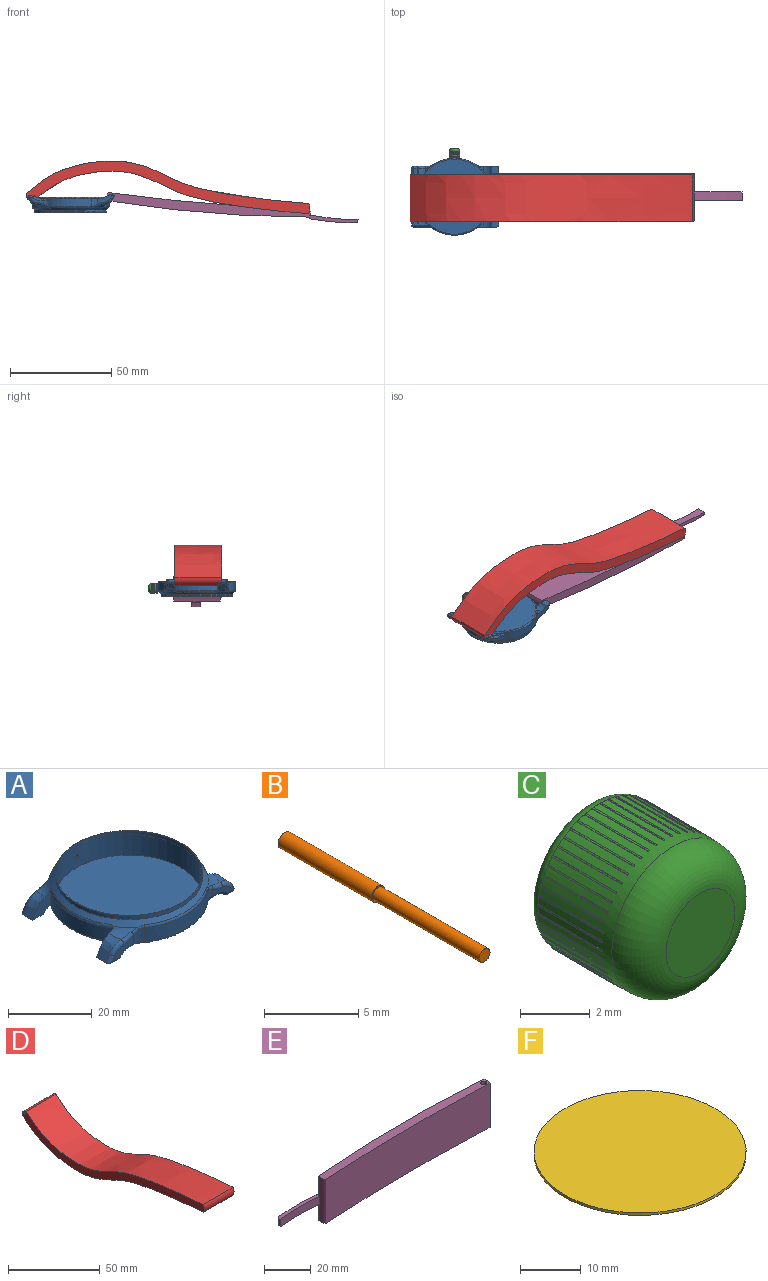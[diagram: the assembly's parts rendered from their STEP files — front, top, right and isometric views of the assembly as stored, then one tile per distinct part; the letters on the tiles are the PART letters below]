
ASSEMBLY  parts=6 mates=5
PART A: 97 faces, bbox 43.8x41.4x10.1 mm
  f0: cylinder r=19mm len=38mm, axis (0,0,-1), area 371.6mm2, adj f1,f3,f13,f14,f20,f21,f25,f27
  f1: plane 3.98x3.54mm, normal (0,0,-1), area 3.8mm2, adj f0,f2,f36,f58
  f2: plane 7.33x4.35mm, normal (0,-1,0), area 16mm2, adj f1,f4,f5,f36,f58,f88,f89,f90
  f3: plane 4.93x1.05mm, normal (-1,0,0), area 1.4mm2, adj f0,f7,f30,f32,f50,f58
  f4: plane 4.45x3.84mm, normal (0,0,-1), area 14.8mm2, adj f2,f5,f6,f7,f90
  f5: plane 4.2x0.04mm, normal (0.73,0,-0.68), area 0.2mm2, adj f2,f4,f7,f58
  f6: plane 3.21x2.46mm, normal (-0.86,0,0.51), area 8.1mm2, adj f4,f7,f54,f90
  f7: plane 6.09x5.88mm, normal (0,1,0), area 18.8mm2, adj f3,f4,f5,f6,f32,f54,f58,f95
  f8: plane 37x37mm, normal (0,0,-1), area 1075.2mm2, adj f94
  f9: plane 3.21x1.26mm, normal (0.86,0,0.51), area 3.6mm2, adj f11,f53,f69,f72
  f10: plane 3.2x1.85mm, normal (0,0,-1), area 5.9mm2, adj f11,f68,f69,f74
  f11: plane 5.88x5.49mm, normal (0,1,0), area 18.2mm2, adj f9,f10,f13,f33,f53,f56,f64,f68
  f12: plane 6.74x3.35mm, normal (0,-1,0), area 8.5mm2, adj f37,f70,f71,f72,f74,f76,f77
  f13: plane 4.93x1.05mm, normal (1,0,0), area 1.4mm2, adj f0,f11,f30,f33,f49,f56
  f14: plane 1.72x1.66mm, normal (0,0,-1), area 1.3mm2, adj f0,f56,f77,f78
  f15: plane 3.21x2.46mm, normal (-0.86,0,0.51), area 8.1mm2, adj f16,f18,f52,f93
  f16: plane 4.45x3.84mm, normal (0,0,-1), area 14.8mm2, adj f15,f17,f18,f19,f93
  f17: plane 4.2x0.04mm, normal (0.73,0,-0.68), area 0.2mm2, adj f16,f18,f19,f57
  f18: plane 6.09x5.88mm, normal (0,-1,0), area 19.3mm2, adj f15,f16,f17,f20,f31,f52,f57
  f19: plane 7.33x4.35mm, normal (0,1,0), area 16mm2, adj f16,f17,f21,f35,f57,f91,f92,f93
  f20: plane 4.93x1.05mm, normal (-1,0,0), area 1.4mm2, adj f0,f18,f30,f31,f50,f57
  f21: plane 3.98x3.54mm, normal (0,0,-1), area 3.8mm2, adj f0,f19,f35,f57
  f22: plane 3.2x1.85mm, normal (0,0,-1), area 5.9mm2, adj f24,f66,f67,f83
  f23: plane 3.21x1.26mm, normal (0.86,0,0.51), area 3.6mm2, adj f24,f51,f66,f81
  f24: plane 5.88x5.49mm, normal (0,-1,0), area 18.2mm2, adj f22,f23,f25,f34,f51,f55,f63,f66
  f25: plane 4.93x1.05mm, normal (1,0,0), area 1.4mm2, adj f0,f24,f30,f34,f49,f55
  f26: plane 6.74x3.35mm, normal (0,1,0), area 8.5mm2, adj f38,f79,f80,f81,f83,f85,f86
  f27: plane 1.72x1.66mm, normal (0,0,-1), area 1.3mm2, adj f0,f55,f86,f87
  f28: cylinder r=17.63mm len=35.27mm, axis (0,0,1), area 125.5mm2, adj f29,f30
  f29: plane 35.27x35.27mm, normal (0,0,1), area 11.5mm2, adj f28,f59
  f30: cone r=17.5mm half-angle=45deg, axis (0,0,-1), area 185mm2, adj f3,f13,f20,f25,f28,f31,f32,f33
  f31: torus R=22.57mm, axis (0,0,1), area 12.7mm2, adj f18,f20,f30,f48,f52,f91
  f32: torus R=22.57mm, axis (0,0,1), area 12.6mm2, adj f3,f7,f30,f39,f54,f88
  f33: torus R=22.57mm, axis (0,0,1), area 12.7mm2, adj f11,f13,f30,f43,f53,f70
  f34: torus R=22.57mm, axis (0,0,1), area 12.6mm2, adj f24,f25,f30,f44,f51,f79
  f35: cylinder r=5mm len=3.84mm, axis (0,0,-1), area 9.9mm2, adj f0,f19,f21,f47,f48
  f36: cylinder r=5mm len=3.84mm, axis (0,0,-1), area 9.9mm2, adj f0,f1,f2,f39,f40
  f37: cylinder r=5mm len=2.84mm, axis (0,0,-1), area 7mm2, adj f0,f12,f42,f43,f78
  f38: cylinder r=5mm len=2.84mm, axis (0,0,-1), area 7mm2, adj f0,f26,f44,f45,f87
  f39: bspline ~2.57x1.81mm, area 1.8mm2, adj f32,f36,f40,f88
  f40: bspline ~3.08x1.77mm, area 1.3mm2, adj f30,f36,f39,f41
  f41: torus R=18mm, axis (0,0,1), area 17.4mm2, adj f0,f30,f40,f42
  f42: bspline ~3.08x1.77mm, area 1.2mm2, adj f30,f37,f41,f43
  f43: bspline ~2.57x1.81mm, area 1.8mm2, adj f33,f37,f42,f70
  f44: bspline ~2.57x1.81mm, area 1.8mm2, adj f34,f38,f45,f79
  f45: bspline ~3.08x1.77mm, area 1.3mm2, adj f30,f38,f44,f46
  f46: torus R=18mm, axis (0,0,1), area 17.4mm2, adj f0,f30,f45,f47
  f47: bspline ~3.08x1.77mm, area 1.2mm2, adj f30,f35,f46,f48
  f48: bspline ~2.57x1.81mm, area 1.8mm2, adj f31,f35,f47,f91
  f49: torus R=18mm, axis (0,0,1), area 17mm2, adj f0,f13,f25,f30
  f50: torus R=18mm, axis (0,0,1), area 17mm2, adj f0,f3,f20,f30
  f51: bspline ~7.25x4.32mm, area 13.7mm2, adj f23,f24,f34,f80
  f52: bspline ~7.25x4.32mm, area 13.7mm2, adj f15,f18,f31,f92
  f53: bspline ~7.25x4.32mm, area 13.7mm2, adj f9,f11,f33,f71
  f54: bspline ~7.25x4.32mm, area 13.7mm2, adj f6,f7,f32,f89
  f55: cylinder r=5mm len=3.52mm, axis (0,-1,0), area 11.5mm2, adj f0,f24,f25,f27,f67,f85
  f56: cylinder r=5mm len=3.52mm, axis (0,-1,0), area 11.5mm2, adj f0,f11,f13,f14,f68,f76
  f57: cylinder r=5mm len=4.52mm, axis (0,-1,0), area 16.4mm2, adj f0,f17,f18,f19,f20,f21
  f58: cylinder r=5mm len=4.52mm, axis (0,-1,0), area 16.4mm2, adj f0,f1,f2,f3,f5,f7
  f59: cylinder r=17.53mm len=35.06mm, axis (0,0,1), area 781.1mm2, adj f29,f60,f61
  f60: plane 35.06x35.06mm, normal (0,0,1), area 965.3mm2, adj f59
  f61: cylinder r=0.53mm len=1.47mm, axis (0,-1,0), area 4.9mm2, adj f0,f59
  f62: plane 0.95x0.95mm, normal (0,-1,0), area 0.7mm2, adj f63
  f63: cylinder r=0.48mm len=3.11mm, axis (0,-1,0), area 9.3mm2, adj f24,f62
  f64: cylinder r=0.48mm len=2.9mm, axis (0,-1,0), area 8.7mm2, adj f11,f65
  f65: plane 0.95x0.95mm, normal (0,1,0), area 0.7mm2, adj f64
  f66: cylinder r=0.8mm len=3.2mm, axis (0,1,0), area 5.4mm2, adj f22,f23,f24,f82
  f67: cylinder r=0.8mm len=3.2mm, axis (0,-1,0), area 2mm2, adj f22,f24,f55,f84
  f68: cylinder r=0.8mm len=3.2mm, axis (0,-1,0), area 2mm2, adj f10,f11,f56,f75
  f69: cylinder r=0.8mm len=3.2mm, axis (0,1,0), area 5.4mm2, adj f9,f10,f11,f73
  f70: bspline ~4.82x1.97mm, area 4.5mm2, adj f12,f33,f43,f71
  f71: bspline ~4.93x3.72mm, area 6.7mm2, adj f12,f53,f70,f72
  f72: cylinder r=1mm len=1.31mm, axis (-0.51,0,0.86), area 1.1mm2, adj f9,f12,f71,f73
  f73: bspline ~1.75x1.21mm, area 1.3mm2, adj f69,f72,f74
  f74: cylinder r=1mm len=1.85mm, axis (1,0,0), area 2.6mm2, adj f10,f12,f73,f75
  f75: bspline ~1.24x1mm, area 0.4mm2, adj f68,f74,f76
  f76: torus R=6mm, axis (0,-1,0), area 6.4mm2, adj f12,f56,f75,f77
  f77: cylinder r=1mm len=1.22mm, axis (-1,0,0), area 1.9mm2, adj f12,f14,f76,f78
  f78: torus R=6mm, axis (0,0,-1), area 2.7mm2, adj f0,f14,f37,f77
  f79: bspline ~4.82x1.97mm, area 4.5mm2, adj f26,f34,f44,f80
  f80: bspline ~4.93x3.72mm, area 6.7mm2, adj f26,f51,f79,f81
  f81: cylinder r=1mm len=1.31mm, axis (0.51,0,-0.86), area 1.1mm2, adj f23,f26,f80,f82
  f82: bspline ~1.75x1.21mm, area 1.3mm2, adj f66,f81,f83
  f83: cylinder r=1mm len=1.85mm, axis (-1,0,0), area 2.6mm2, adj f22,f26,f82,f84
  f84: bspline ~1.24x1mm, area 0.4mm2, adj f67,f83,f85
  f85: torus R=6mm, axis (0,-1,0), area 6.4mm2, adj f26,f55,f84,f86
  f86: cylinder r=1mm len=1.22mm, axis (1,0,0), area 1.9mm2, adj f26,f27,f85,f87
  f87: torus R=6mm, axis (0,0,-1), area 2.7mm2, adj f0,f27,f38,f86
  f88: bspline ~4.82x1.97mm, area 4.5mm2, adj f2,f32,f39,f89
  f89: bspline ~4.97x3.81mm, area 6.7mm2, adj f2,f54,f88,f90
  f90: cylinder r=1mm len=2.48mm, axis (0.51,0,0.86), area 3.1mm2, adj f2,f4,f6,f89
  f91: bspline ~4.82x1.97mm, area 4.5mm2, adj f19,f31,f48,f92
  f92: bspline ~4.97x3.81mm, area 6.7mm2, adj f19,f52,f91,f93
  f93: cylinder r=1mm len=2.48mm, axis (-0.51,0,-0.86), area 3.1mm2, adj f15,f16,f19,f92
  f94: torus R=18.5mm, axis (0,0,1), area 92.9mm2, adj f0,f8
  f95: cylinder r=0.41mm len=3mm, axis (0,1,0), area 7.6mm2, adj f7,f96
  f96: plane 0.81x0.81mm, normal (0,1,0), area 0.5mm2, adj f95
PART B: 5 faces, bbox 1x15x1 mm
  f0: cylinder r=0.5mm len=7mm, axis (0,1,0), area 21.9mm2, adj f1,f3
  f1: plane 1x1mm, normal (0,1,0), area 0.8mm2, adj f0
  f2: cylinder r=0.42mm len=8mm, axis (0,-1,0), area 20.9mm2, adj f3,f4
  f3: plane 1x1mm, normal (0,-1,0), area 0.2mm2, adj f0,f2
  f4: plane 0.83x0.83mm, normal (0,-1,0), area 0.5mm2, adj f2
PART C: 257 faces, bbox 5.4x4.5x5.4 mm
  f0: cylinder r=2.5mm len=5mm, axis (0,1,0), area 40.6mm2, adj f3,f4,f7,f8,f9,f11,f12,f13
  f1: plane 2.8x2.8mm, normal (0,-1,0), area 6.2mm2, adj f3
  f2: plane 4.2x4.2mm, normal (0,1,0), area 13.1mm2, adj f4,f5
  f3: torus R=1.4mm, axis (0,-1,0), area 22.8mm2, adj f0,f1
  f4: torus R=2.1mm, axis (0,-1,0), area 9.3mm2, adj f0,f2
  f5: cylinder r=0.5mm len=3mm, axis (0,1,0), area 9.4mm2, adj f2,f6
  f6: plane 1x1mm, normal (0,1,0), area 0.8mm2, adj f5
  f7: plane 2.6x0.02mm, normal (1,0,0), area 0.1mm2, adj f0,f9,f10,f11
  f8: plane 2.6x0.02mm, normal (-1,0,0), area 0mm2, adj f0,f9,f10,f11
  f9: plane 0.05x0.02mm, normal (0,1,0), area 0mm2, adj f0,f7,f8,f10
  f10: plane 2.6x0.05mm, normal (0,0,1), area 0.1mm2, adj f7,f8,f9,f11
  f11: plane 0.05x0.02mm, normal (0,-1,0), area 0mm2, adj f0,f7,f8,f10
  f12: plane 2.6x0.02mm, normal (0.99,0,0.13), area 0.1mm2, adj f0,f14,f15,f16
  f13: plane 2.6x0.02mm, normal (-0.99,0,-0.13), area 0mm2, adj f0,f14,f15,f16
  f14: plane 0.05x0.03mm, normal (0,1,0), area 0mm2, adj f0,f12,f13,f15
  f15: plane 2.6x0.05mm, normal (-0.13,0,0.99), area 0.1mm2, adj f12,f13,f14,f16
  f16: plane 0.05x0.03mm, normal (0,-1,0), area 0mm2, adj f0,f12,f13,f15
  f17: plane 2.6x0.02mm, normal (0.97,0,0.25), area 0.1mm2, adj f0,f19,f20,f21
  f18: plane 2.6x0.02mm, normal (-0.97,0,-0.25), area 0mm2, adj f0,f19,f20,f21
  f19: plane 0.05x0.03mm, normal (0,1,0), area 0mm2, adj f0,f17,f18,f20
  f20: plane 2.6x0.05mm, normal (-0.25,0,0.97), area 0.1mm2, adj f17,f18,f19,f21
  f21: plane 0.05x0.03mm, normal (0,-1,0), area 0mm2, adj f0,f17,f18,f20
  f22: plane 2.6x0.02mm, normal (0.93,0,0.37), area 0.1mm2, adj f0,f24,f25,f26
  f23: plane 2.6x0.02mm, normal (-0.93,0,-0.37), area 0mm2, adj f0,f24,f25,f26
  f24: plane 0.05x0.04mm, normal (0,1,0), area 0mm2, adj f0,f22,f23,f25
  f25: plane 2.6x0.05mm, normal (-0.37,0,0.93), area 0.1mm2, adj f22,f23,f24,f26
  f26: plane 0.05x0.04mm, normal (0,-1,0), area 0mm2, adj f0,f22,f23,f25
  f27: plane 2.6x0.02mm, normal (0.88,0,0.48), area 0.1mm2, adj f0,f29,f30,f31
  f28: plane 2.6x0.02mm, normal (-0.88,0,-0.48), area 0mm2, adj f0,f29,f30,f31
  f29: plane 0.05x0.04mm, normal (0,1,0), area 0mm2, adj f0,f27,f28,f30
  f30: plane 2.6x0.04mm, normal (-0.48,0,0.88), area 0.1mm2, adj f27,f28,f29,f31
  f31: plane 0.05x0.04mm, normal (0,-1,0), area 0mm2, adj f0,f27,f28,f30
  f32: plane 2.6x0.02mm, normal (0.81,0,0.59), area 0.1mm2, adj f0,f34,f35,f36
  f33: plane 2.6x0.02mm, normal (-0.81,0,-0.59), area 0mm2, adj f0,f34,f35,f36
  f34: plane 0.05x0.04mm, normal (0,1,0), area 0mm2, adj f0,f32,f33,f35
  f35: plane 2.6x0.04mm, normal (-0.59,0,0.81), area 0.1mm2, adj f32,f33,f34,f36
  f36: plane 0.05x0.04mm, normal (0,-1,0), area 0mm2, adj f0,f32,f33,f35
  f37: plane 2.6x0.01mm, normal (0.73,0,0.68), area 0.1mm2, adj f0,f39,f40,f41
  f38: plane 2.6x0.01mm, normal (-0.73,0,-0.68), area 0mm2, adj f0,f39,f40,f41
  f39: plane 0.05x0.05mm, normal (0,1,0), area 0mm2, adj f0,f37,f38,f40
  f40: plane 2.6x0.04mm, normal (-0.68,0,0.73), area 0.1mm2, adj f37,f38,f39,f41
  f41: plane 0.05x0.05mm, normal (0,-1,0), area 0mm2, adj f0,f37,f38,f40
  f42: plane 2.6x0.02mm, normal (0.64,0,0.77), area 0.1mm2, adj f0,f44,f45,f46
  f43: plane 2.6x0.01mm, normal (-0.64,0,-0.77), area 0mm2, adj f0,f44,f45,f46
  f44: plane 0.05x0.05mm, normal (0,1,0), area 0mm2, adj f0,f42,f43,f45
  f45: plane 2.6x0.04mm, normal (-0.77,0,0.64), area 0.1mm2, adj f42,f43,f44,f46
  f46: plane 0.05x0.05mm, normal (0,-1,0), area 0mm2, adj f0,f42,f43,f45
  f47: plane 2.6x0.02mm, normal (0.54,0,0.84), area 0.1mm2, adj f0,f49,f50,f51
  f48: plane 2.6x0.02mm, normal (-0.54,0,-0.84), area 0mm2, adj f0,f49,f50,f51
  f49: plane 0.05x0.04mm, normal (0,1,0), area 0mm2, adj f0,f47,f48,f50
  f50: plane 2.6x0.04mm, normal (-0.84,0,0.54), area 0.1mm2, adj f47,f48,f49,f51
  f51: plane 0.05x0.04mm, normal (0,-1,0), area 0mm2, adj f0,f47,f48,f50
  f52: plane 2.6x0.02mm, normal (0.43,0,0.9), area 0.1mm2, adj f0,f54,f55,f56
  f53: plane 2.6x0.02mm, normal (-0.43,0,-0.9), area 0mm2, adj f0,f54,f55,f56
  f54: plane 0.05x0.04mm, normal (0,1,0), area 0mm2, adj f0,f52,f53,f55
  f55: plane 2.6x0.05mm, normal (-0.9,0,0.43), area 0.1mm2, adj f52,f53,f54,f56
  f56: plane 0.05x0.04mm, normal (0,-1,0), area 0mm2, adj f0,f52,f53,f55
  f57: plane 2.6x0.02mm, normal (0.31,0,0.95), area 0.1mm2, adj f0,f59,f60,f61
  f58: plane 2.6x0.02mm, normal (-0.31,0,-0.95), area 0mm2, adj f0,f59,f60,f61
  f59: plane 0.05x0.03mm, normal (0,1,0), area 0mm2, adj f0,f57,f58,f60
  f60: plane 2.6x0.05mm, normal (-0.95,0,0.31), area 0.1mm2, adj f57,f58,f59,f61
  f61: plane 0.05x0.03mm, normal (0,-1,0), area 0mm2, adj f0,f57,f58,f60
  f62: plane 2.6x0.02mm, normal (0.19,0,0.98), area 0.1mm2, adj f0,f64,f65,f66
  f63: plane 2.6x0.02mm, normal (-0.19,0,-0.98), area 0mm2, adj f0,f64,f65,f66
  f64: plane 0.05x0.03mm, normal (0,1,0), area 0mm2, adj f0,f62,f63,f65
  f65: plane 2.6x0.05mm, normal (-0.98,0,0.19), area 0.1mm2, adj f62,f63,f64,f66
  f66: plane 0.05x0.03mm, normal (0,-1,0), area 0mm2, adj f0,f62,f63,f65
  f67: plane 2.6x0.02mm, normal (0.06,0,1), area 0.1mm2, adj f0,f69,f70,f71
  f68: plane 2.6x0.02mm, normal (-0.06,0,-1), area 0mm2, adj f0,f69,f70,f71
  f69: plane 0.05x0.02mm, normal (0,1,0), area 0mm2, adj f0,f67,f68,f70
  f70: plane 2.6x0.05mm, normal (-1,0,0.06), area 0.1mm2, adj f67,f68,f69,f71
  f71: plane 0.05x0.02mm, normal (0,-1,0), area 0mm2, adj f0,f67,f68,f70
  f72: plane 2.6x0.02mm, normal (-0.06,0,1), area 0.1mm2, adj f0,f74,f75,f76
  f73: plane 2.6x0.02mm, normal (0.06,0,-1), area 0mm2, adj f0,f74,f75,f76
  f74: plane 0.05x0.02mm, normal (0,1,0), area 0mm2, adj f0,f72,f73,f75
  f75: plane 2.6x0.05mm, normal (-1,0,-0.06), area 0.1mm2, adj f72,f73,f74,f76
  f76: plane 0.05x0.02mm, normal (0,-1,0), area 0mm2, adj f0,f72,f73,f75
  f77: plane 2.6x0.02mm, normal (-0.19,0,0.98), area 0.1mm2, adj f0,f79,f80,f81
  f78: plane 2.6x0.02mm, normal (0.19,0,-0.98), area 0mm2, adj f0,f79,f80,f81
  f79: plane 0.05x0.03mm, normal (0,1,0), area 0mm2, adj f0,f77,f78,f80
  f80: plane 2.6x0.05mm, normal (-0.98,0,-0.19), area 0.1mm2, adj f77,f78,f79,f81
  f81: plane 0.05x0.03mm, normal (0,-1,0), area 0mm2, adj f0,f77,f78,f80
  f82: plane 2.6x0.02mm, normal (-0.31,0,0.95), area 0.1mm2, adj f0,f84,f85,f86
  f83: plane 2.6x0.02mm, normal (0.31,0,-0.95), area 0mm2, adj f0,f84,f85,f86
  f84: plane 0.05x0.03mm, normal (0,1,0), area 0mm2, adj f0,f82,f83,f85
  f85: plane 2.6x0.05mm, normal (-0.95,0,-0.31), area 0.1mm2, adj f82,f83,f84,f86
  f86: plane 0.05x0.03mm, normal (0,-1,0), area 0mm2, adj f0,f82,f83,f85
  f87: plane 2.6x0.02mm, normal (-0.43,0,0.9), area 0.1mm2, adj f0,f89,f90,f91
  f88: plane 2.6x0.02mm, normal (0.43,0,-0.9), area 0mm2, adj f0,f89,f90,f91
  f89: plane 0.05x0.04mm, normal (0,1,0), area 0mm2, adj f0,f87,f88,f90
  f90: plane 2.6x0.05mm, normal (-0.9,0,-0.43), area 0.1mm2, adj f87,f88,f89,f91
  f91: plane 0.05x0.04mm, normal (0,-1,0), area 0mm2, adj f0,f87,f88,f90
  f92: plane 2.6x0.02mm, normal (-0.54,0,0.84), area 0.1mm2, adj f0,f94,f95,f96
  f93: plane 2.6x0.02mm, normal (0.54,0,-0.84), area 0mm2, adj f0,f94,f95,f96
  f94: plane 0.05x0.04mm, normal (0,1,0), area 0mm2, adj f0,f92,f93,f95
  f95: plane 2.6x0.04mm, normal (-0.84,0,-0.54), area 0.1mm2, adj f92,f93,f94,f96
  f96: plane 0.05x0.04mm, normal (0,-1,0), area 0mm2, adj f0,f92,f93,f95
  f97: plane 2.6x0.02mm, normal (-0.64,0,0.77), area 0.1mm2, adj f0,f99,f100,f101
  f98: plane 2.6x0.01mm, normal (0.64,0,-0.77), area 0mm2, adj f0,f99,f100,f101
  f99: plane 0.05x0.05mm, normal (0,1,0), area 0mm2, adj f0,f97,f98,f100
  f100: plane 2.6x0.04mm, normal (-0.77,0,-0.64), area 0.1mm2, adj f97,f98,f99,f101
  f101: plane 0.05x0.05mm, normal (0,-1,0), area 0mm2, adj f0,f97,f98,f100
  f102: plane 2.6x0.01mm, normal (-0.73,0,0.68), area 0.1mm2, adj f0,f104,f105,f106
  f103: plane 2.6x0.01mm, normal (0.73,0,-0.68), area 0mm2, adj f0,f104,f105,f106
  f104: plane 0.05x0.05mm, normal (0,1,0), area 0mm2, adj f0,f102,f103,f105
  f105: plane 2.6x0.04mm, normal (-0.68,0,-0.73), area 0.1mm2, adj f102,f103,f104,f106
  f106: plane 0.05x0.05mm, normal (0,-1,0), area 0mm2, adj f0,f102,f103,f105
  f107: plane 2.6x0.02mm, normal (-0.81,0,0.59), area 0.1mm2, adj f0,f109,f110,f111
  f108: plane 2.6x0.02mm, normal (0.81,0,-0.59), area 0mm2, adj f0,f109,f110,f111
  f109: plane 0.05x0.05mm, normal (0,1,0), area 0mm2, adj f0,f107,f108,f110
  f110: plane 2.6x0.04mm, normal (-0.59,0,-0.81), area 0.1mm2, adj f107,f108,f109,f111
  f111: plane 0.05x0.05mm, normal (0,-1,0), area 0mm2, adj f0,f107,f108,f110
  f112: plane 2.6x0.02mm, normal (-0.88,0,0.48), area 0.1mm2, adj f0,f114,f115,f116
  f113: plane 2.6x0.02mm, normal (0.88,0,-0.48), area 0mm2, adj f0,f114,f115,f116
  f114: plane 0.05x0.04mm, normal (0,1,0), area 0mm2, adj f0,f112,f113,f115
  f115: plane 2.6x0.04mm, normal (-0.48,0,-0.88), area 0.1mm2, adj f112,f113,f114,f116
  f116: plane 0.05x0.04mm, normal (0,-1,0), area 0mm2, adj f0,f112,f113,f115
  f117: plane 2.6x0.02mm, normal (-0.93,0,0.37), area 0.1mm2, adj f0,f119,f120,f121
  f118: plane 2.6x0.02mm, normal (0.93,0,-0.37), area 0mm2, adj f0,f119,f120,f121
  f119: plane 0.05x0.04mm, normal (0,1,0), area 0mm2, adj f0,f117,f118,f120
  f120: plane 2.6x0.05mm, normal (-0.37,0,-0.93), area 0.1mm2, adj f117,f118,f119,f121
  f121: plane 0.05x0.04mm, normal (0,-1,0), area 0mm2, adj f0,f117,f118,f120
  f122: plane 2.6x0.02mm, normal (-0.97,0,0.25), area 0.1mm2, adj f0,f124,f125,f126
  f123: plane 2.6x0.02mm, normal (0.97,0,-0.25), area 0mm2, adj f0,f124,f125,f126
  f124: plane 0.05x0.03mm, normal (0,1,0), area 0mm2, adj f0,f122,f123,f125
  f125: plane 2.6x0.05mm, normal (-0.25,0,-0.97), area 0.1mm2, adj f122,f123,f124,f126
  f126: plane 0.05x0.03mm, normal (0,-1,0), area 0mm2, adj f0,f122,f123,f125
  f127: plane 2.6x0.02mm, normal (-0.99,0,0.13), area 0.1mm2, adj f0,f129,f130,f131
  f128: plane 2.6x0.02mm, normal (0.99,0,-0.13), area 0mm2, adj f0,f129,f130,f131
  f129: plane 0.05x0.03mm, normal (0,1,0), area 0mm2, adj f0,f127,f128,f130
  f130: plane 2.6x0.05mm, normal (-0.13,0,-0.99), area 0.1mm2, adj f127,f128,f129,f131
  f131: plane 0.05x0.03mm, normal (0,-1,0), area 0mm2, adj f0,f127,f128,f130
  f132: plane 2.6x0.02mm, normal (-1,0,0), area 0.1mm2, adj f0,f134,f135,f136
  f133: plane 2.6x0.02mm, normal (1,0,0), area 0mm2, adj f0,f134,f135,f136
  f134: plane 0.05x0.02mm, normal (0,1,0), area 0mm2, adj f0,f132,f133,f135
  f135: plane 2.6x0.05mm, normal (0,0,-1), area 0.1mm2, adj f132,f133,f134,f136
  f136: plane 0.05x0.02mm, normal (0,-1,0), area 0mm2, adj f0,f132,f133,f135
  f137: plane 2.6x0.02mm, normal (-0.99,0,-0.13), area 0.1mm2, adj f0,f139,f140,f141
  f138: plane 2.6x0.02mm, normal (0.99,0,0.13), area 0mm2, adj f0,f139,f140,f141
  f139: plane 0.05x0.03mm, normal (0,1,0), area 0mm2, adj f0,f137,f138,f140
  f140: plane 2.6x0.05mm, normal (0.13,0,-0.99), area 0.1mm2, adj f137,f138,f139,f141
  f141: plane 0.05x0.03mm, normal (0,-1,0), area 0mm2, adj f0,f137,f138,f140
  f142: plane 2.6x0.02mm, normal (-0.97,0,-0.25), area 0.1mm2, adj f0,f144,f145,f146
  f143: plane 2.6x0.02mm, normal (0.97,0,0.25), area 0mm2, adj f0,f144,f145,f146
  f144: plane 0.05x0.03mm, normal (0,1,0), area 0mm2, adj f0,f142,f143,f145
  f145: plane 2.6x0.05mm, normal (0.25,0,-0.97), area 0.1mm2, adj f142,f143,f144,f146
  f146: plane 0.05x0.03mm, normal (0,-1,0), area 0mm2, adj f0,f142,f143,f145
  f147: plane 2.6x0.02mm, normal (-0.93,0,-0.37), area 0.1mm2, adj f0,f149,f150,f151
  f148: plane 2.6x0.02mm, normal (0.93,0,0.37), area 0mm2, adj f0,f149,f150,f151
  f149: plane 0.05x0.04mm, normal (0,1,0), area 0mm2, adj f0,f147,f148,f150
  f150: plane 2.6x0.05mm, normal (0.37,0,-0.93), area 0.1mm2, adj f147,f148,f149,f151
  f151: plane 0.05x0.04mm, normal (0,-1,0), area 0mm2, adj f0,f147,f148,f150
  f152: plane 2.6x0.02mm, normal (-0.88,0,-0.48), area 0.1mm2, adj f0,f154,f155,f156
  f153: plane 2.6x0.02mm, normal (0.88,0,0.48), area 0mm2, adj f0,f154,f155,f156
  f154: plane 0.05x0.04mm, normal (0,1,0), area 0mm2, adj f0,f152,f153,f155
  f155: plane 2.6x0.04mm, normal (0.48,0,-0.88), area 0.1mm2, adj f152,f153,f154,f156
  f156: plane 0.05x0.04mm, normal (0,-1,0), area 0mm2, adj f0,f152,f153,f155
  f157: plane 2.6x0.02mm, normal (-0.81,0,-0.59), area 0.1mm2, adj f0,f159,f160,f161
  f158: plane 2.6x0.02mm, normal (0.81,0,0.59), area 0mm2, adj f0,f159,f160,f161
  f159: plane 0.05x0.04mm, normal (0,1,0), area 0mm2, adj f0,f157,f158,f160
  f160: plane 2.6x0.04mm, normal (0.59,0,-0.81), area 0.1mm2, adj f157,f158,f159,f161
  f161: plane 0.05x0.04mm, normal (0,-1,0), area 0mm2, adj f0,f157,f158,f160
  f162: plane 2.6x0.01mm, normal (-0.73,0,-0.68), area 0.1mm2, adj f0,f164,f165,f166
  f163: plane 2.6x0.01mm, normal (0.73,0,0.68), area 0mm2, adj f0,f164,f165,f166
  f164: plane 0.05x0.05mm, normal (0,1,0), area 0mm2, adj f0,f162,f163,f165
  f165: plane 2.6x0.04mm, normal (0.68,0,-0.73), area 0.1mm2, adj f162,f163,f164,f166
  f166: plane 0.05x0.05mm, normal (0,-1,0), area 0mm2, adj f0,f162,f163,f165
  f167: plane 2.6x0.02mm, normal (-0.64,0,-0.77), area 0.1mm2, adj f0,f169,f170,f171
  f168: plane 2.6x0.01mm, normal (0.64,0,0.77), area 0mm2, adj f0,f169,f170,f171
  f169: plane 0.05x0.05mm, normal (0,1,0), area 0mm2, adj f0,f167,f168,f170
  f170: plane 2.6x0.04mm, normal (0.77,0,-0.64), area 0.1mm2, adj f167,f168,f169,f171
  f171: plane 0.05x0.05mm, normal (0,-1,0), area 0mm2, adj f0,f167,f168,f170
  f172: plane 2.6x0.02mm, normal (-0.54,0,-0.84), area 0.1mm2, adj f0,f174,f175,f176
  f173: plane 2.6x0.02mm, normal (0.54,0,0.84), area 0mm2, adj f0,f174,f175,f176
  f174: plane 0.05x0.04mm, normal (0,1,0), area 0mm2, adj f0,f172,f173,f175
  f175: plane 2.6x0.04mm, normal (0.84,0,-0.54), area 0.1mm2, adj f172,f173,f174,f176
  f176: plane 0.05x0.04mm, normal (0,-1,0), area 0mm2, adj f0,f172,f173,f175
  f177: plane 2.6x0.02mm, normal (-0.43,0,-0.9), area 0.1mm2, adj f0,f179,f180,f181
  f178: plane 2.6x0.02mm, normal (0.43,0,0.9), area 0mm2, adj f0,f179,f180,f181
  f179: plane 0.05x0.04mm, normal (0,1,0), area 0mm2, adj f0,f177,f178,f180
  f180: plane 2.6x0.05mm, normal (0.9,0,-0.43), area 0.1mm2, adj f177,f178,f179,f181
  f181: plane 0.05x0.04mm, normal (0,-1,0), area 0mm2, adj f0,f177,f178,f180
  f182: plane 2.6x0.02mm, normal (-0.31,0,-0.95), area 0.1mm2, adj f0,f184,f185,f186
  f183: plane 2.6x0.02mm, normal (0.31,0,0.95), area 0mm2, adj f0,f184,f185,f186
  f184: plane 0.05x0.03mm, normal (0,1,0), area 0mm2, adj f0,f182,f183,f185
  f185: plane 2.6x0.05mm, normal (0.95,0,-0.31), area 0.1mm2, adj f182,f183,f184,f186
  f186: plane 0.05x0.03mm, normal (0,-1,0), area 0mm2, adj f0,f182,f183,f185
  f187: plane 2.6x0.02mm, normal (-0.19,0,-0.98), area 0.1mm2, adj f0,f189,f190,f191
  f188: plane 2.6x0.02mm, normal (0.19,0,0.98), area 0mm2, adj f0,f189,f190,f191
  f189: plane 0.05x0.03mm, normal (0,1,0), area 0mm2, adj f0,f187,f188,f190
  f190: plane 2.6x0.05mm, normal (0.98,0,-0.19), area 0.1mm2, adj f187,f188,f189,f191
  f191: plane 0.05x0.03mm, normal (0,-1,0), area 0mm2, adj f0,f187,f188,f190
  f192: plane 2.6x0.02mm, normal (-0.06,0,-1), area 0.1mm2, adj f0,f194,f195,f196
  f193: plane 2.6x0.02mm, normal (0.06,0,1), area 0mm2, adj f0,f194,f195,f196
  f194: plane 0.05x0.02mm, normal (0,1,0), area 0mm2, adj f0,f192,f193,f195
  f195: plane 2.6x0.05mm, normal (1,0,-0.06), area 0.1mm2, adj f192,f193,f194,f196
  f196: plane 0.05x0.02mm, normal (0,-1,0), area 0mm2, adj f0,f192,f193,f195
  f197: plane 2.6x0.02mm, normal (0.06,0,-1), area 0.1mm2, adj f0,f199,f200,f201
  f198: plane 2.6x0.02mm, normal (-0.06,0,1), area 0mm2, adj f0,f199,f200,f201
  f199: plane 0.05x0.02mm, normal (0,1,0), area 0mm2, adj f0,f197,f198,f200
  f200: plane 2.6x0.05mm, normal (1,0,0.06), area 0.1mm2, adj f197,f198,f199,f201
  f201: plane 0.05x0.02mm, normal (0,-1,0), area 0mm2, adj f0,f197,f198,f200
  f202: plane 2.6x0.02mm, normal (0.19,0,-0.98), area 0.1mm2, adj f0,f204,f205,f206
  f203: plane 2.6x0.02mm, normal (-0.19,0,0.98), area 0mm2, adj f0,f204,f205,f206
  f204: plane 0.05x0.03mm, normal (0,1,0), area 0mm2, adj f0,f202,f203,f205
  f205: plane 2.6x0.05mm, normal (0.98,0,0.19), area 0.1mm2, adj f202,f203,f204,f206
  f206: plane 0.05x0.03mm, normal (0,-1,0), area 0mm2, adj f0,f202,f203,f205
  f207: plane 2.6x0.02mm, normal (0.31,0,-0.95), area 0.1mm2, adj f0,f209,f210,f211
  f208: plane 2.6x0.02mm, normal (-0.31,0,0.95), area 0mm2, adj f0,f209,f210,f211
  f209: plane 0.05x0.03mm, normal (0,1,0), area 0mm2, adj f0,f207,f208,f210
  f210: plane 2.6x0.05mm, normal (0.95,0,0.31), area 0.1mm2, adj f207,f208,f209,f211
  f211: plane 0.05x0.03mm, normal (0,-1,0), area 0mm2, adj f0,f207,f208,f210
  f212: plane 2.6x0.02mm, normal (0.43,0,-0.9), area 0.1mm2, adj f0,f214,f215,f216
  f213: plane 2.6x0.02mm, normal (-0.43,0,0.9), area 0mm2, adj f0,f214,f215,f216
  f214: plane 0.05x0.04mm, normal (0,1,0), area 0mm2, adj f0,f212,f213,f215
  f215: plane 2.6x0.05mm, normal (0.9,0,0.43), area 0.1mm2, adj f212,f213,f214,f216
  f216: plane 0.05x0.04mm, normal (0,-1,0), area 0mm2, adj f0,f212,f213,f215
  f217: plane 2.6x0.02mm, normal (0.54,0,-0.84), area 0.1mm2, adj f0,f219,f220,f221
  f218: plane 2.6x0.02mm, normal (-0.54,0,0.84), area 0mm2, adj f0,f219,f220,f221
  f219: plane 0.05x0.04mm, normal (0,1,0), area 0mm2, adj f0,f217,f218,f220
  f220: plane 2.6x0.04mm, normal (0.84,0,0.54), area 0.1mm2, adj f217,f218,f219,f221
  f221: plane 0.05x0.04mm, normal (0,-1,0), area 0mm2, adj f0,f217,f218,f220
  f222: plane 2.6x0.02mm, normal (0.64,0,-0.77), area 0.1mm2, adj f0,f224,f225,f226
  f223: plane 2.6x0.01mm, normal (-0.64,0,0.77), area 0mm2, adj f0,f224,f225,f226
  f224: plane 0.05x0.05mm, normal (0,1,0), area 0mm2, adj f0,f222,f223,f225
  f225: plane 2.6x0.04mm, normal (0.77,0,0.64), area 0.1mm2, adj f222,f223,f224,f226
  f226: plane 0.05x0.05mm, normal (0,-1,0), area 0mm2, adj f0,f222,f223,f225
  f227: plane 2.6x0.01mm, normal (0.73,0,-0.68), area 0.1mm2, adj f0,f229,f230,f231
  f228: plane 2.6x0.01mm, normal (-0.73,0,0.68), area 0mm2, adj f0,f229,f230,f231
  f229: plane 0.05x0.05mm, normal (0,1,0), area 0mm2, adj f0,f227,f228,f230
  f230: plane 2.6x0.04mm, normal (0.68,0,0.73), area 0.1mm2, adj f227,f228,f229,f231
  f231: plane 0.05x0.05mm, normal (0,-1,0), area 0mm2, adj f0,f227,f228,f230
  f232: plane 2.6x0.02mm, normal (0.81,0,-0.59), area 0.1mm2, adj f0,f234,f235,f236
  f233: plane 2.6x0.02mm, normal (-0.81,0,0.59), area 0mm2, adj f0,f234,f235,f236
  f234: plane 0.05x0.05mm, normal (0,1,0), area 0mm2, adj f0,f232,f233,f235
  f235: plane 2.6x0.04mm, normal (0.59,0,0.81), area 0.1mm2, adj f232,f233,f234,f236
  f236: plane 0.05x0.05mm, normal (0,-1,0), area 0mm2, adj f0,f232,f233,f235
  f237: plane 2.6x0.02mm, normal (0.88,0,-0.48), area 0.1mm2, adj f0,f239,f240,f241
  f238: plane 2.6x0.02mm, normal (-0.88,0,0.48), area 0mm2, adj f0,f239,f240,f241
  f239: plane 0.05x0.04mm, normal (0,1,0), area 0mm2, adj f0,f237,f238,f240
  f240: plane 2.6x0.04mm, normal (0.48,0,0.88), area 0.1mm2, adj f237,f238,f239,f241
  f241: plane 0.05x0.04mm, normal (0,-1,0), area 0mm2, adj f0,f237,f238,f240
  f242: plane 2.6x0.02mm, normal (0.93,0,-0.37), area 0.1mm2, adj f0,f244,f245,f246
  f243: plane 2.6x0.02mm, normal (-0.93,0,0.37), area 0mm2, adj f0,f244,f245,f246
  f244: plane 0.05x0.04mm, normal (0,1,0), area 0mm2, adj f0,f242,f243,f245
  f245: plane 2.6x0.05mm, normal (0.37,0,0.93), area 0.1mm2, adj f242,f243,f244,f246
  f246: plane 0.05x0.04mm, normal (0,-1,0), area 0mm2, adj f0,f242,f243,f245
  f247: plane 2.6x0.02mm, normal (0.97,0,-0.25), area 0.1mm2, adj f0,f249,f250,f251
  f248: plane 2.6x0.02mm, normal (-0.97,0,0.25), area 0mm2, adj f0,f249,f250,f251
  f249: plane 0.05x0.03mm, normal (0,1,0), area 0mm2, adj f0,f247,f248,f250
  f250: plane 2.6x0.05mm, normal (0.25,0,0.97), area 0.1mm2, adj f247,f248,f249,f251
  f251: plane 0.05x0.03mm, normal (0,-1,0), area 0mm2, adj f0,f247,f248,f250
  f252: plane 2.6x0.02mm, normal (0.99,0,-0.13), area 0.1mm2, adj f0,f254,f255,f256
  f253: plane 2.6x0.02mm, normal (-0.99,0,0.13), area 0mm2, adj f0,f254,f255,f256
  f254: plane 0.05x0.03mm, normal (0,1,0), area 0mm2, adj f0,f252,f253,f255
  f255: plane 2.6x0.05mm, normal (0.13,0,0.99), area 0.1mm2, adj f252,f253,f254,f256
  f256: plane 0.05x0.03mm, normal (0,-1,0), area 0mm2, adj f0,f252,f253,f255
PART D: 7 faces, bbox 23x140.2x27.9 mm
  f0: extruded ~139.73x23mm, area 3377.8mm2, adj f1,f3,f4,f5
  f1: cylinder r=3.55mm len=23mm, axis (-1,0,0), area 127.6mm2, adj f0,f2,f4,f5
  f2: extruded ~136.3x23mm, area 3291.7mm2, adj f1,f3,f4,f5
  f3: cylinder r=5.64mm len=23mm, axis (-1,0,0), area 119.1mm2, adj f0,f2,f4,f5
  f4: plane 140.21x27.85mm, normal (1,0,0), area 729.1mm2, adj f0,f1,f2,f3,f6
  f5: plane 140.21x27.85mm, normal (-1,0,0), area 729.1mm2, adj f0,f1,f2,f3,f6
  f6: cylinder r=0.7mm len=23mm, axis (-1,0,0), area 100.7mm2, adj f4,f5
PART E: 14 faces, bbox 124.5x6.3x23 mm
  f0: cylinder r=5.89mm len=23mm, axis (0,0,-1), area 95.4mm2, adj f1,f3,f4,f5
  f1: cylinder r=641.37mm len=100.35mm, axis (0,0,-1), area 2309.8mm2, adj f0,f2,f4,f5,f7,f12,f13
  f2: cylinder r=5.66mm len=23mm, axis (0,0,-1), area 88.7mm2, adj f1,f3,f4,f5,f8,f12,f13
  f3: cylinder r=902.99mm len=99.78mm, axis (0,0,-1), area 2296.1mm2, adj f0,f2,f4,f5
  f4: plane 100.81x6.31mm, normal (0,0,1), area 436mm2, adj f0,f1,f2,f3,f6
  f5: plane 100.81x6.31mm, normal (0,0,-1), area 436mm2, adj f0,f1,f2,f3,f6
  f6: cylinder r=1.31mm len=23mm, axis (0,0,1), area 188.7mm2, adj f4,f5
  f7: cylinder r=0.82mm len=4mm, axis (0,0,-1), area 4.8mm2, adj f1,f10,f12,f13
  f8: cylinder r=113mm len=23.74mm, axis (0,0,-1), area 95.1mm2, adj f2,f9,f12,f13
  f9: plane 4x1.05mm, normal (-1,0,0), area 4.2mm2, adj f8,f11,f12,f13
  f10: cylinder r=123.5mm len=22.63mm, axis (0,0,-1), area 90.6mm2, adj f7,f11,f12,f13
  f11: cylinder r=0.82mm len=4mm, axis (0,0,-1), area 4.9mm2, adj f9,f10,f12,f13
  f12: plane 24.12x2.39mm, normal (0,0,1), area 41.9mm2, adj f1,f2,f7,f8,f9,f10,f11
  f13: plane 24.12x2.39mm, normal (0,0,-1), area 41.9mm2, adj f1,f2,f7,f8,f9,f10,f11
PART F: 3 faces, bbox 35.1x35.1x0.5 mm
  f0: cylinder r=17.53mm len=35.06mm, axis (0,0,-1), area 55.1mm2, adj f1,f2
  f1: plane 35.06x35.06mm, normal (0,0,1), area 965.3mm2, adj f0
  f2: plane 35.06x35.06mm, normal (0,0,-1), area 965.3mm2, adj f0
PLACE A rot(axis=(0,1,0),179.7deg) t=(-50.31,54.34,-44.74)mm
PLACE B rot(axis=(0,0,-1),180deg) t=(-50.31,60.6,-44.74)mm
PLACE C rot(axis=(0,0,-1),180deg) t=(-50.31,73.5,-44.74)mm
PLACE D rot(axis=(0.71,-0.71,0),180deg) t=(-72.33,65.09,-39.47)mm
PLACE E rot(axis=(0.03,-0.71,0.71),176.4deg) t=(28.22,65.68,-50.8)mm
PLACE F rot(axis=(0,1,0),179.7deg) t=(-50.31,54.34,-44.49)mm
MATE revolute C.f0 <-> B.f0  axis (0,-1,0) through (-50.31,73.5,-44.74)mm
MATE cylindrical E.f6 <-> A.f95  axis (0,-1,0) through (-30.32,65.68,-41.19)mm
MATE revolute B.f0 <-> A.f61  axis (0,1,0) through (-50.31,71.6,-44.74)mm
MATE revolute F.f0 <-> A.f0  axis (0,0,-1) through (-50.29,54.34,-48.74)mm
MATE cylindrical D.f6 <-> A.f63  axis (0,1,0) through (-70.23,65.09,-41.35)mm
